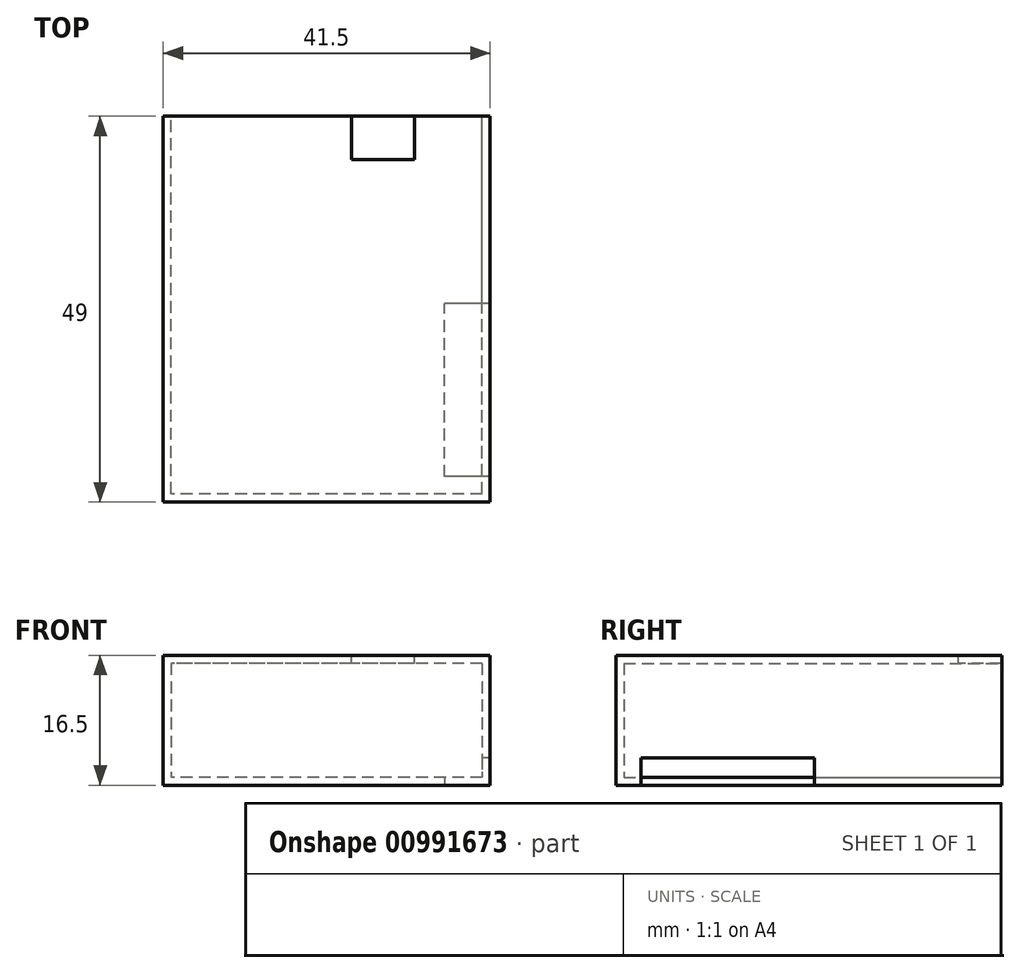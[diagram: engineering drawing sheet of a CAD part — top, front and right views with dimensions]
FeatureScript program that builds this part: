
annotation { "Feature Type Name" : "Feature", "Feature Type Description" : "" }
export const myFeature = defineFeature(function(context is Context, id is Id, definition is map)
    precondition{}
    {
        {
            var Q0;
            Q0=qCreatedBy(makeId("Top.planeOp"),FACE);
            var sketch = newSketch(context, id + "F0", { "sketchPlane" : qUnion([Q0])});
            skLineSegment(sketch, "E0.bottom", {"start": v(-40.83, 14.31) * mm, "end": v(0.67, 14.31) * mm});
            skLineSegment(sketch, "E0.top", {"start": v(-40.83, -34.69) * mm, "end": v(0.67, -34.69) * mm});
            skLineSegment(sketch, "E0.left", {"start": v(-40.83, 14.31) * mm, "end": v(-40.83, -34.69) * mm});
            skLineSegment(sketch, "E0.right", {"start": v(0.67, 14.31) * mm, "end": v(0.67, -34.69) * mm});
            skSolve(sketch);
        }
        {
            var Q0;
            Q0=makeQuery(id+"F0.imprint","IMPRINT",FACE,{"disambiguationData":[TD([[makeQuery(id+"F0.imprint","IMPRINT",EDGE,{"derivedFrom":sQuery(id+"F0.wireOp",EDGE,"E0.bottom")}),-1.0]])]});
            extrude(context, id + "F1", {"entities" : qUnion([Q0]), "depth" : 16.5 * mm, "offsetDistance" : 25 * mm});
        }
        {
            var Q0;
            Q0=makeQuery(id+"F1.opExtrude","SWEPT_FACE",FACE,{"disambiguationData":[OSD([sQuery(id+"F0.wireOp",EDGE,"E0.bottom")])]});
            var sketch = newSketch(context, id + "F2", { "sketchPlane" : qUnion([Q0])});
            skLineSegment(sketch, "E1.bottom", {"start": v(0.31, 15.5) * mm, "end": v(39.81, 15.5) * mm});
            skLineSegment(sketch, "E1.top", {"start": v(0.31, 1) * mm, "end": v(39.81, 1) * mm});
            skLineSegment(sketch, "E1.left", {"start": v(0.31, 15.5) * mm, "end": v(0.31, 1) * mm});
            skLineSegment(sketch, "E1.right", {"start": v(39.81, 15.5) * mm, "end": v(39.81, 1) * mm});
            skLineSegment(sketch, "E2", {"start": v(20.06, 1) * mm, "end": v(20.06, 15.5) * mm, "construction": true});
            skLineSegment(sketch, "E3", {"start": v(0.31, 8.25) * mm, "end": v(39.81, 8.25) * mm, "construction": true});
            skLineSegment(sketch, "E4", {"start": v(20.08, 16.5) * mm, "end": v(20.08, 0) * mm, "construction": true});
            skLineSegment(sketch, "E5", {"start": v(40.83, 8.25) * mm, "end": v(-0.67, 8.25) * mm, "construction": true});
            skSolve(sketch);
        }
        {
            var Q0;
            Q0=makeQuery(id+"F2.imprint","IMPRINT",FACE,{"disambiguationData":[TD([[makeQuery(id+"F2.imprint","IMPRINT",EDGE,{"derivedFrom":sQuery(id+"F2.wireOp",EDGE,"E1.bottom")}),-1.0]])]});
            extrude(context, id + "F3", {"entities" : qUnion([Q0]), "operationType" : NewBodyOperationType.REMOVE, "oppositeDirection" : true, "depth" : 48 * mm, "offsetDistance" : 25 * mm});
        }
        {
            var Q0;
            Q0=makeQuery(id+"F1.opExtrude","CAP_FACE",FACE,{"disambiguationData":[OSD([sQuery(id+"F0.wireOp",EDGE,"E0.bottom"),sQuery(id+"F0.wireOp",EDGE,"E0.top"),sQuery(id+"F0.wireOp",EDGE,"E0.left"),sQuery(id+"F0.wireOp",EDGE,"E0.right")])],"isStart":false});
            var sketch = newSketch(context, id + "F4", { "sketchPlane" : qUnion([Q0])});
            skLineSegment(sketch, "E6", {"start": v(0.67, 13.9) * mm, "end": v(-8.95, 13.9) * mm, "construction": true});
            skLineSegment(sketch, "E7.bottom", {"start": v(-8.95, 14.31) * mm, "end": v(-16.95, 14.31) * mm});
            skLineSegment(sketch, "E7.top", {"start": v(-8.95, 8.81) * mm, "end": v(-16.95, 8.81) * mm});
            skLineSegment(sketch, "E7.left", {"start": v(-8.95, 14.31) * mm, "end": v(-8.95, 8.81) * mm});
            skLineSegment(sketch, "E7.right", {"start": v(-16.95, 14.31) * mm, "end": v(-16.95, 8.81) * mm});
            skSolve(sketch);
        }
        {
            var Q0;
            Q0=makeQuery(id+"F4.imprint","IMPRINT",FACE,{"disambiguationData":[TD([[makeQuery(id+"F4.imprint","IMPRINT",EDGE,{"derivedFrom":sQuery(id+"F4.wireOp",EDGE,"E7.bottom")}),-1.0]])]});
            extrude(context, id + "F5", {"entities" : qUnion([Q0]), "operationType" : NewBodyOperationType.REMOVE, "endBound" : BoundingType.UP_TO_NEXT, "oppositeDirection" : true, "depth" : 25 * mm, "offsetDistance" : 25 * mm});
        }
        {
            var Q0;
            Q0=makeQuery(id+"F1.opExtrude","CAP_FACE",FACE,{"disambiguationData":[OSD([sQuery(id+"F0.wireOp",EDGE,"E0.bottom"),sQuery(id+"F0.wireOp",EDGE,"E0.top"),sQuery(id+"F0.wireOp",EDGE,"E0.left"),sQuery(id+"F0.wireOp",EDGE,"E0.right")])],"isStart":true});
            var sketch = newSketch(context, id + "F6", { "sketchPlane" : qUnion([Q0])});
            skLineSegment(sketch, "E8", {"start": v(-3.01, 34.69) * mm, "end": v(-3.01, 31.49) * mm, "construction": true});
            skLineSegment(sketch, "E9.bottom", {"start": v(0.67, 31.49) * mm, "end": v(-5.08, 31.49) * mm});
            skLineSegment(sketch, "E9.top", {"start": v(0.67, 9.49) * mm, "end": v(-5.08, 9.49) * mm});
            skLineSegment(sketch, "E9.left", {"start": v(0.67, 31.49) * mm, "end": v(0.67, 9.49) * mm});
            skLineSegment(sketch, "E9.right", {"start": v(-5.08, 31.49) * mm, "end": v(-5.08, 9.49) * mm});
            skSolve(sketch);
        }
        {
            var Q0;
            Q0=makeQuery(id+"F6.imprint","IMPRINT",FACE,{"disambiguationData":[TD([[makeQuery(id+"F6.imprint","IMPRINT",EDGE,{"derivedFrom":sQuery(id+"F6.wireOp",EDGE,"E9.bottom")}),1.0]])]});
            extrude(context, id + "F7", {"entities" : qUnion([Q0]), "operationType" : NewBodyOperationType.REMOVE, "oppositeDirection" : true, "depth" : 3.5 * mm, "offsetDistance" : 25 * mm});
        }
    });
